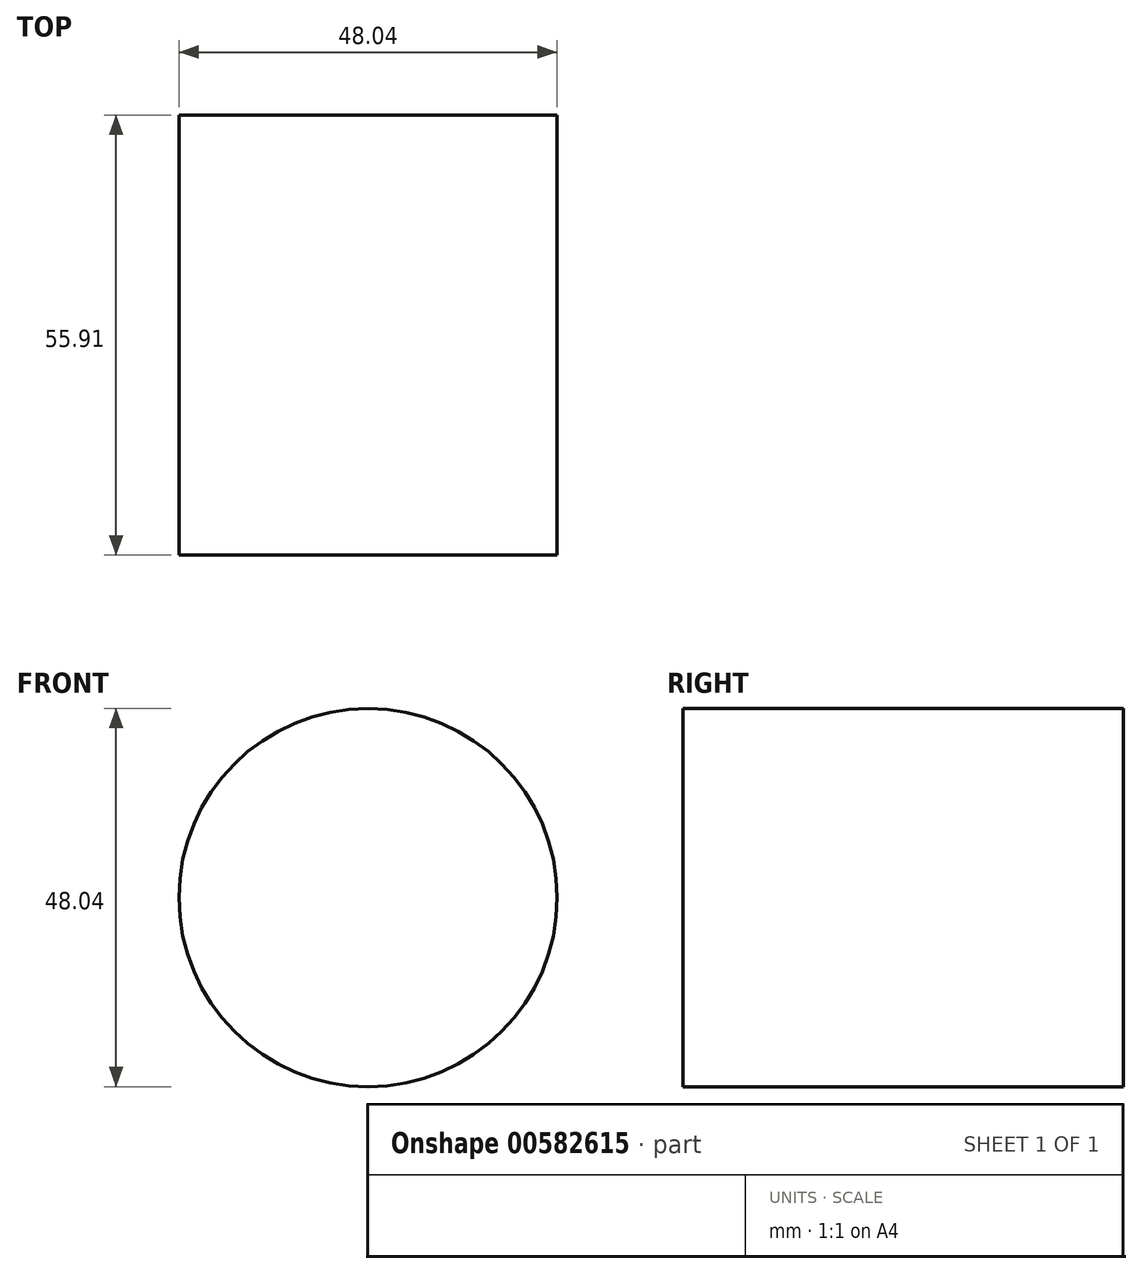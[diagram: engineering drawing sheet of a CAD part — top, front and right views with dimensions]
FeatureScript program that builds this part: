
annotation { "Feature Type Name" : "Feature", "Feature Type Description" : "" }
export const myFeature = defineFeature(function(context is Context, id is Id, definition is map)
    precondition{}
    {
        {
            var Q0;
            Q0=qCreatedBy(makeId("Front.planeOp"),FACE);
            var sketch = newSketch(context, id + "F0", { "sketchPlane" : qUnion([Q0])});
            skCircle(sketch, "E0", {"center": v(0, 0) * mm, "radius": 24.02 * mm});
            skSolve(sketch);
        }
        {
            var Q0;
            Q0=sQuery(id+"F0.wireOp",EDGE,"E0");
            extrude(context, id + "F1", {"bodyType" : ToolBodyType.SURFACE, "surfaceEntities" : qUnion([Q0]), "depth" : 55.9 * mm, "offsetDistance" : 25.4 * mm});
        }
    });
